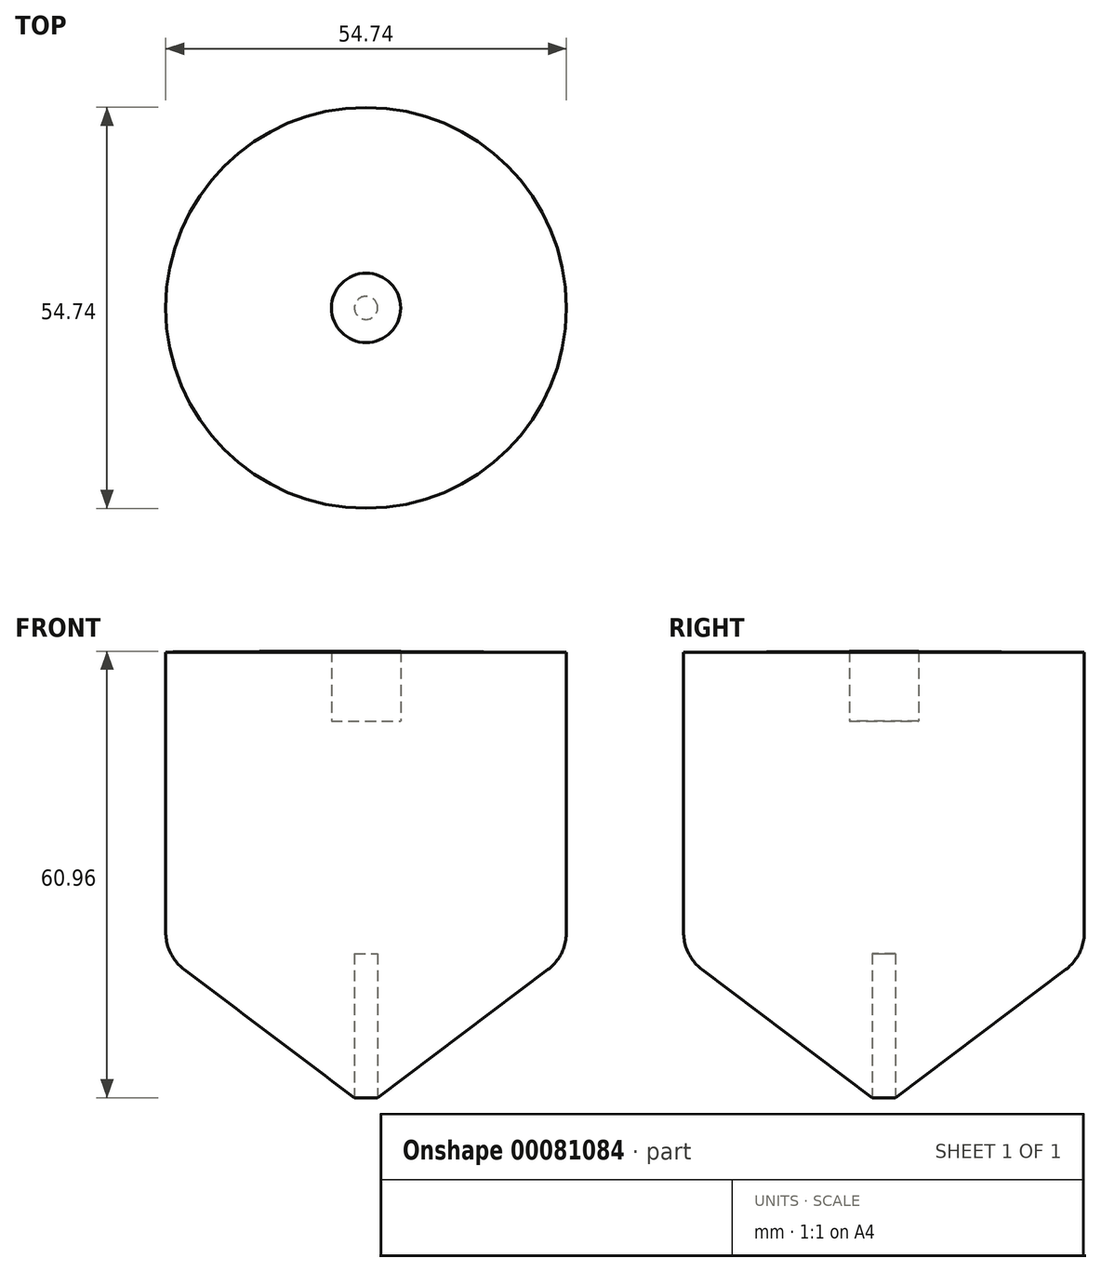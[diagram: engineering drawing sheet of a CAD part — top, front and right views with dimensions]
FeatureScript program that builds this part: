
annotation { "Feature Type Name" : "Feature", "Feature Type Description" : "" }
export const myFeature = defineFeature(function(context is Context, id is Id, definition is map)
    precondition{}
    {
        {
            var Q0;
            Q0=qCreatedBy(makeId("Front.planeOp"),FACE);
            var sketch = newSketch(context, id + "F0", { "sketchPlane" : qUnion([Q0])});
            skLineSegment(sketch, "E0", {"start": v(0, 0) * mm, "end": v(0, 63.5) * mm});
            skLineSegment(sketch, "E1", {"start": v(-1.59, 0) * mm, "end": v(-1.59, 22.23) * mm});
            skLineSegment(sketch, "E2", {"start": v(-1.59, 22.23) * mm, "end": v(0, 22.23) * mm});
            skLineSegment(sketch, "E3", {"start": v(0, 22.23) * mm, "end": v(-1.59, 22.23) * mm});
            skLineSegment(sketch, "E4", {"start": v(-4.73, 63.5) * mm, "end": v(-4.73, 63.5) * mm});
            skLineSegment(sketch, "E5", {"start": v(-1.59, 0) * mm, "end": v(-63.5, 0) * mm});
            skPoint(sketch, "E6.orphan", {"position": v(-9.81, 0) * mm});
            skLineSegment(sketch, "E7", {"start": v(-4.73, 63.5) * mm, "end": v(-4.73, 53.98) * mm});
            skLineSegment(sketch, "E8", {"start": v(-4.73, 53.98) * mm, "end": v(0, 53.98) * mm});
            skLineSegment(sketch, "E9", {"start": v(0, 53.98) * mm, "end": v(-36.83, 53.98) * mm});
            skLineSegment(sketch, "E10", {"start": v(-1.59, 0) * mm, "end": v(-1.59, 2.54) * mm});
            skLineSegment(sketch, "E11", {"start": v(-1.59, 2.54) * mm, "end": v(-27.37, 21.93) * mm});
            skLineSegment(sketch, "E12", {"start": v(-27.37, 21.93) * mm, "end": v(-27.37, 63.38) * mm});
            skLineSegment(sketch, "E13", {"start": v(-27.37, 63.38) * mm, "end": v(-4.73, 63.5) * mm});
            skSolve(sketch);
        }
        {
            var Q0;
            Q0=makeQuery(id+"F0.imprint","IMPRINT",FACE,{"disambiguationData":[TD([[makeQuery(id+"F0.imprint","IMPRINT",EDGE,{"derivedFrom":sQuery(id+"F0.wireOp",EDGE,"E1")}),1.0]])]});
            var Q1;
            {var subQ0=sQuery(id+"F0.wireOp",EDGE,"E7");Q1=makeQuery(id+"F0.imprint","IMPRINT",FACE,{"disambiguationData":[TD([[makeQuery(id+"F0.imprint","IMPRINT",EDGE,{"derivedFrom":subQ0}),-1.0]])]});}
            var Q2;
            Q2=sQuery(id+"F0.wireOp",EDGE,"E0");
            revolve(context, id + "F1", {"entities" : qUnion([Q0, Q1]), "axis" : qUnion([Q2]), "revolveType" : RevolveType.FULL});
        }
        {
            var Q0;
            Q0=makeQuery(id+"F1.opRevolve","SWEPT_EDGE",EDGE,{"disambiguationData":[OSD([sQuery(id+"F0.wireOp",EDGE,"E11"),sQuery(id+"F0.wireOp",EDGE,"E12")])]});
            fillet(context, id + "F2", {"entities" : qUnion([Q0]), "radius" : 6.35 * mm, "tangentPropagation" : true, "allowEdgeOverflow" : false});
        }
    });
